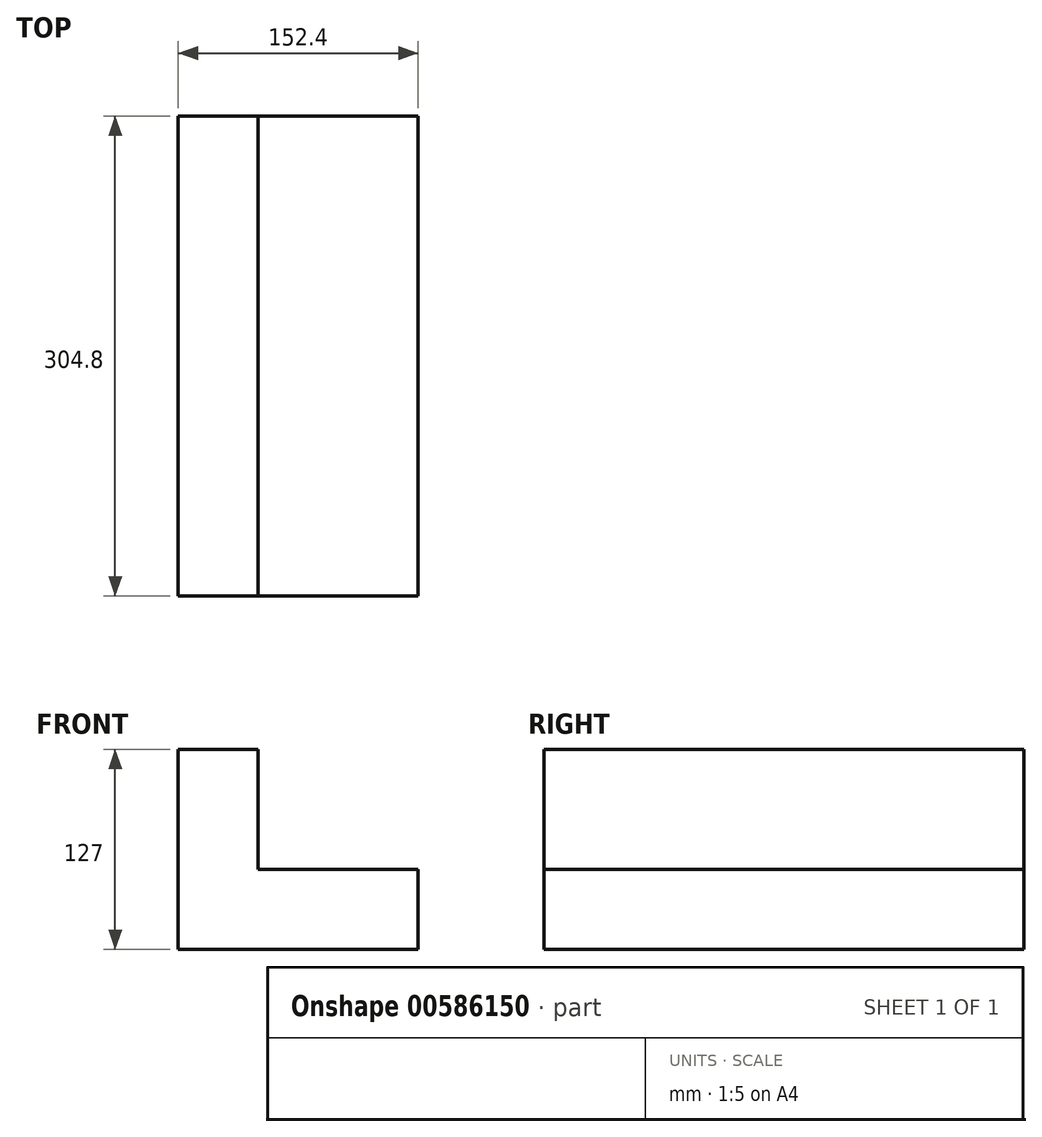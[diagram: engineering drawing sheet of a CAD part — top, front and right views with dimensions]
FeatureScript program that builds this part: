
annotation { "Feature Type Name" : "Feature", "Feature Type Description" : "" }
export const myFeature = defineFeature(function(context is Context, id is Id, definition is map)
    precondition{}
    {
        {
            var Q0;
            Q0=qCreatedBy(makeId("Front.planeOp"),FACE);
            var sketch = newSketch(context, id + "F0", { "sketchPlane" : qUnion([Q0])});
            skLineSegment(sketch, "E0.bottom", {"start": v(0, 0) * mm, "end": v(50.8, 0) * mm});
            skLineSegment(sketch, "E0.top", {"start": v(0, 127) * mm, "end": v(50.8, 127) * mm});
            skLineSegment(sketch, "E0.left", {"start": v(0, 0) * mm, "end": v(0, 127) * mm});
            skLineSegment(sketch, "E0.right", {"start": v(50.8, 0) * mm, "end": v(50.8, 127) * mm});
            skLineSegment(sketch, "E1.bottom", {"start": v(50.8, 0) * mm, "end": v(152.4, 0) * mm});
            skLineSegment(sketch, "E1.top", {"start": v(50.8, 50.8) * mm, "end": v(152.4, 50.8) * mm});
            skLineSegment(sketch, "E1.left", {"start": v(50.8, 0) * mm, "end": v(50.8, 50.8) * mm});
            skLineSegment(sketch, "E1.right", {"start": v(152.4, 0) * mm, "end": v(152.4, 50.8) * mm});
            skSolve(sketch);
        }
        {
            var Q0;
            Q0 = qSketchRegion(id + "F0", true);
            extrude(context, id + "F1", {"entities" : qUnion([Q0]), "depth" : 304.8 * mm, "offsetDistance" : 25.4 * mm});
        }
    });
